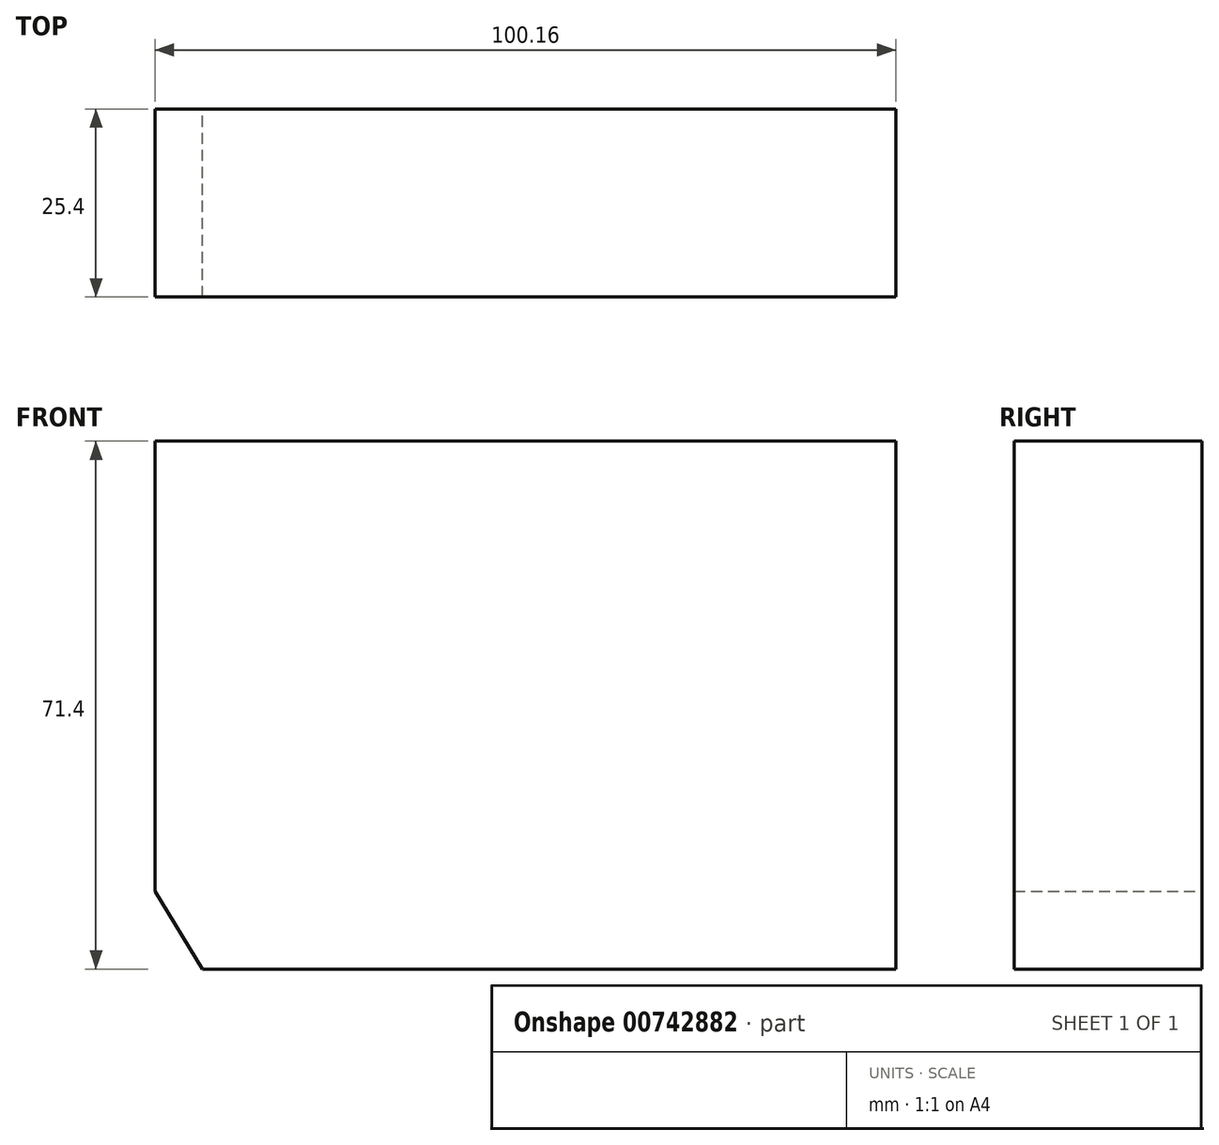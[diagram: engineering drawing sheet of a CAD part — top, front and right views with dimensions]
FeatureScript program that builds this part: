
annotation { "Feature Type Name" : "Feature", "Feature Type Description" : "" }
export const myFeature = defineFeature(function(context is Context, id is Id, definition is map)
    precondition{}
    {
        {
            var Q0;
            Q0=qCreatedBy(makeId("Front.planeOp"),FACE);
            var sketch = newSketch(context, id + "F0", { "sketchPlane" : qUnion([Q0])});
            skLineSegment(sketch, "E0", {"start": v(-49.2, 0) * mm, "end": v(-49.2, -45.12) * mm});
            skLineSegment(sketch, "E1", {"start": v(-49.2, -45.12) * mm, "end": v(-35.19, -45.12) * mm});
            skLineSegment(sketch, "E2", {"start": v(-35.19, -45.12) * mm, "end": v(-35.19, 0) * mm});
            skLineSegment(sketch, "E3", {"start": v(-35.19, 0) * mm, "end": v(-49.2, 0) * mm});
            skLineSegment(sketch, "E4", {"start": v(-49.2, -45.12) * mm, "end": v(-49.2, -60.88) * mm});
            skLineSegment(sketch, "E5", {"start": v(-49.2, -60.88) * mm, "end": v(33.43, -60.88) * mm});
            skLineSegment(sketch, "E6", {"start": v(33.43, -60.88) * mm, "end": v(33.43, 0) * mm});
            skLineSegment(sketch, "E7", {"start": v(33.43, 0) * mm, "end": v(-35.19, 0) * mm});
            skLineSegment(sketch, "E8", {"start": v(-49.2, -60.88) * mm, "end": v(-42.78, -71.4) * mm});
            skLineSegment(sketch, "E9", {"start": v(-42.78, -71.4) * mm, "end": v(33.43, -71.4) * mm});
            skLineSegment(sketch, "E10", {"start": v(33.43, -71.4) * mm, "end": v(33.43, -60.88) * mm});
            skLineSegment(sketch, "E11", {"start": v(33.43, -71.4) * mm, "end": v(50.96, -71.4) * mm});
            skLineSegment(sketch, "E12", {"start": v(50.96, -71.4) * mm, "end": v(50.96, 0) * mm});
            skLineSegment(sketch, "E13", {"start": v(50.96, 0) * mm, "end": v(33.43, 0) * mm});
            skSolve(sketch);
        }
        {
            var Q0;
            Q0 = qSketchRegion(id + "F0", true);
            extrude(context, id + "F1", {"entities" : qUnion([Q0]), "depth" : 25.4 * mm, "offsetDistance" : 25.4 * mm});
        }
    });
